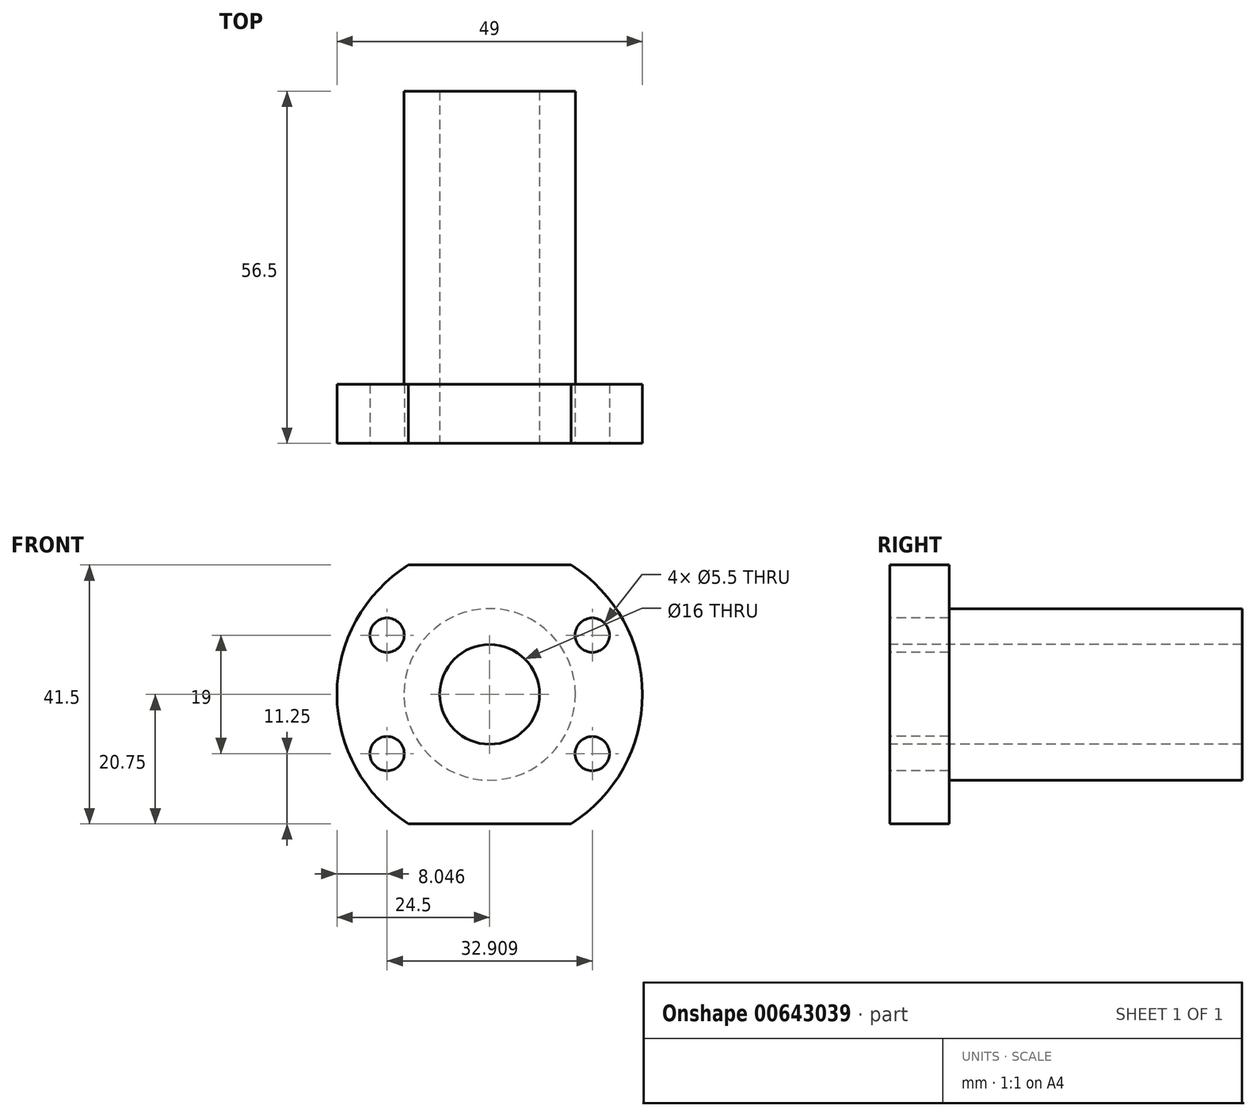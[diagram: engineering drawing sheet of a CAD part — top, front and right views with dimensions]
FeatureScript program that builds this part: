
annotation { "Feature Type Name" : "Feature", "Feature Type Description" : "" }
export const myFeature = defineFeature(function(context is Context, id is Id, definition is map)
    precondition{}
    {
        {
            var Q0;
            Q0=qCreatedBy(makeId("Front.planeOp"),FACE);
            var sketch = newSketch(context, id + "F0", { "sketchPlane" : qUnion([Q0])});
            skCircle(sketch, "E0", {"center": v(0, 0) * mm, "radius": 13.75 * mm});
            skSolve(sketch);
        }
        {
            var Q0;
            Q0=makeQuery(id+"F0.imprint","IMPRINT",FACE,{"disambiguationData":[TD([[makeQuery(id+"F0.imprint","IMPRINT",EDGE,{"derivedFrom":sQuery(id+"F0.wireOp",EDGE,"E0")}),1.0]])]});
            extrude(context, id + "F1", {"entities" : qUnion([Q0]), "depth" : 47 * mm, "offsetDistance" : 25 * mm});
        }
        {
            var Q0;
            Q0=makeQuery(id+"F1.opExtrude","CAP_FACE",FACE,{"disambiguationData":[OSD([sQuery(id+"F0.wireOp",EDGE,"E0")])],"isStart":false});
            var sketch = newSketch(context, id + "F2", { "sketchPlane" : qUnion([Q0])});
            skArc(sketch, "E1", {"start": v(-13.03, 20.75) * mm, "mid": v(-24.5, 0) * mm, "end": v(-13.03, -20.75) * mm});
            skLineSegment(sketch, "E2", {"start": v(-13.03, 20.75) * mm, "end": v(13.03, 20.75) * mm});
            skLineSegment(sketch, "E3", {"start": v(-24.5, 0) * mm, "end": v(24.5, 0) * mm, "construction": true});
            skLineSegment(sketch, "E4.MirrorCS", {"start": v(-13.03, -20.75) * mm, "end": v(13.03, -20.75) * mm});
            skArc(sketch, "E5.trimOffspring", {"start": v(13.03, -20.75) * mm, "mid": v(24.5, 0) * mm, "end": v(13.03, 20.75) * mm});
            skSolve(sketch);
        }
        {
            var Q0;
            Q0=makeQuery(id+"F2.imprint","IMPRINT",FACE,{"disambiguationData":[TD([[makeQuery(id+"F2.imprint","IMPRINT",EDGE,{"derivedFrom":sQuery(id+"F2.wireOp",EDGE,"E1")}),1.0]])]});
            var Q1;
            Q1=makeQuery(id+"F2.imprint","IMPRINT",FACE,{"disambiguationData":[TD([[makeQuery(id+"F2.imprint","IMPRINT",EDGE,{"derivedFrom":makeQuery(id+"F1.opExtrude","CAP_EDGE",EDGE,{"disambiguationData":[OSD([sQuery(id+"F0.wireOp",EDGE,"E0")])],"isStart":false})}),1.0]])]});
            extrude(context, id + "F3", {"entities" : qUnion([Q0, Q1]), "operationType" : NewBodyOperationType.ADD, "depth" : 9.5 * mm, "offsetDistance" : 25 * mm});
        }
        {
            var Q0;
            Q0=makeQuery(id+"F3.opExtrude","CAP_FACE",FACE,{"disambiguationData":[OSD([sQuery(id+"F2.wireOp",EDGE,"E1"),sQuery(id+"F2.wireOp",EDGE,"E2"),sQuery(id+"F2.wireOp",EDGE,"E4.MirrorCS"),sQuery(id+"F2.wireOp",EDGE,"E5.trimOffspring")])],"isStart":false});
            var sketch = newSketch(context, id + "F4", { "sketchPlane" : qUnion([Q0])});
            skCircle(sketch, "E6", {"center": v(0, 0) * mm, "radius": 8 * mm});
            skSolve(sketch);
        }
        {
            var Q0;
            Q0=makeQuery(id+"F4.imprint","IMPRINT",FACE,{"disambiguationData":[TD([[makeQuery(id+"F4.imprint","IMPRINT",EDGE,{"derivedFrom":sQuery(id+"F4.wireOp",EDGE,"E6")}),1.0]])]});
            extrude(context, id + "F5", {"entities" : qUnion([Q0]), "operationType" : NewBodyOperationType.REMOVE, "endBound" : BoundingType.THROUGH_ALL, "oppositeDirection" : true, "depth" : 25 * mm, "offsetDistance" : 25 * mm});
        }
        {
            var Q0;
            Q0=makeQuery(id+"F3.opExtrude","CAP_FACE",FACE,{"disambiguationData":[OSD([sQuery(id+"F2.wireOp",EDGE,"E1"),sQuery(id+"F2.wireOp",EDGE,"E2"),sQuery(id+"F2.wireOp",EDGE,"E4.MirrorCS"),sQuery(id+"F2.wireOp",EDGE,"E5.trimOffspring")])],"isStart":false});
            var sketch = newSketch(context, id + "F6", { "sketchPlane" : qUnion([Q0])});
            skCircle(sketch, "E7", {"center": v(0, 0) * mm, "radius": 19 * mm, "construction": true});
            skLineSegment(sketch, "E8", {"start": v(0, 0) * mm, "end": v(-24.5, 0) * mm, "construction": true});
            skPoint(sketch, "E8.endSnap0", {"position": v(-24.5, 0) * mm});
            skPoint(sketch, "E9.orphan", {"position": v(-40.3, 0) * mm});
            skLineSegment(sketch, "E10", {"start": v(0, 0) * mm, "end": v(-21.22, 12.25) * mm, "construction": true});
            skPoint(sketch, "E11", {"position": v(-16.45, 9.5) * mm});
            skPoint(sketch, "E12.MirrorP", {"position": v(-16.45, -9.5) * mm});
            skLineSegment(sketch, "E13", {"start": v(0, 0) * mm, "end": v(0, -19) * mm, "construction": true});
            skPoint(sketch, "E14.MirrorP", {"position": v(16.45, -9.5) * mm});
            skPoint(sketch, "E15.MirrorP", {"position": v(16.45, 9.5) * mm});
            skSolve(sketch);
        }
        {
            var Q0;
            Q0=sQuery(id+"F6.wireOp",VERTEX,"E11");
            var Q1;
            Q1=sQuery(id+"F6.wireOp",VERTEX,"E12.MirrorP");
            var Q2;
            Q2=sQuery(id+"F6.wireOp",VERTEX,"E15.MirrorP");
            var Q3;
            Q3=sQuery(id+"F6.wireOp",VERTEX,"E14.MirrorP");
            var Q4;
            Q4=makeQuery(id+"F1.opExtrude","SWEPT_BODY",BODY,{"disambiguationData":[OSD([sQuery(id+"F0.wireOp",EDGE,"E0")])]});
            hole(context, id + "F7", {"style" : HoleStyle.SIMPLE, "endStyle" : HoleEndStyle.THROUGH, "standardTappedOrClearance" : lookupTablePath({ "standard" : "ISO", "fit" : "Normal", "size" : "M5", "type" : "Clearance" }), "standardBlindInLast" : lookupTablePath({ "fit" : "Standard", "standard" : "ISO", "size" : "M5", "type" : "Clearance" }), "holeDiameter" : 5.5 * mm, "tappedDepth" : 12 * mm, "tapClearance" : 3, "locations" : qUnion([Q0, Q1, Q2, Q3]), "scope" : qUnion([Q4])});
        }
    });
